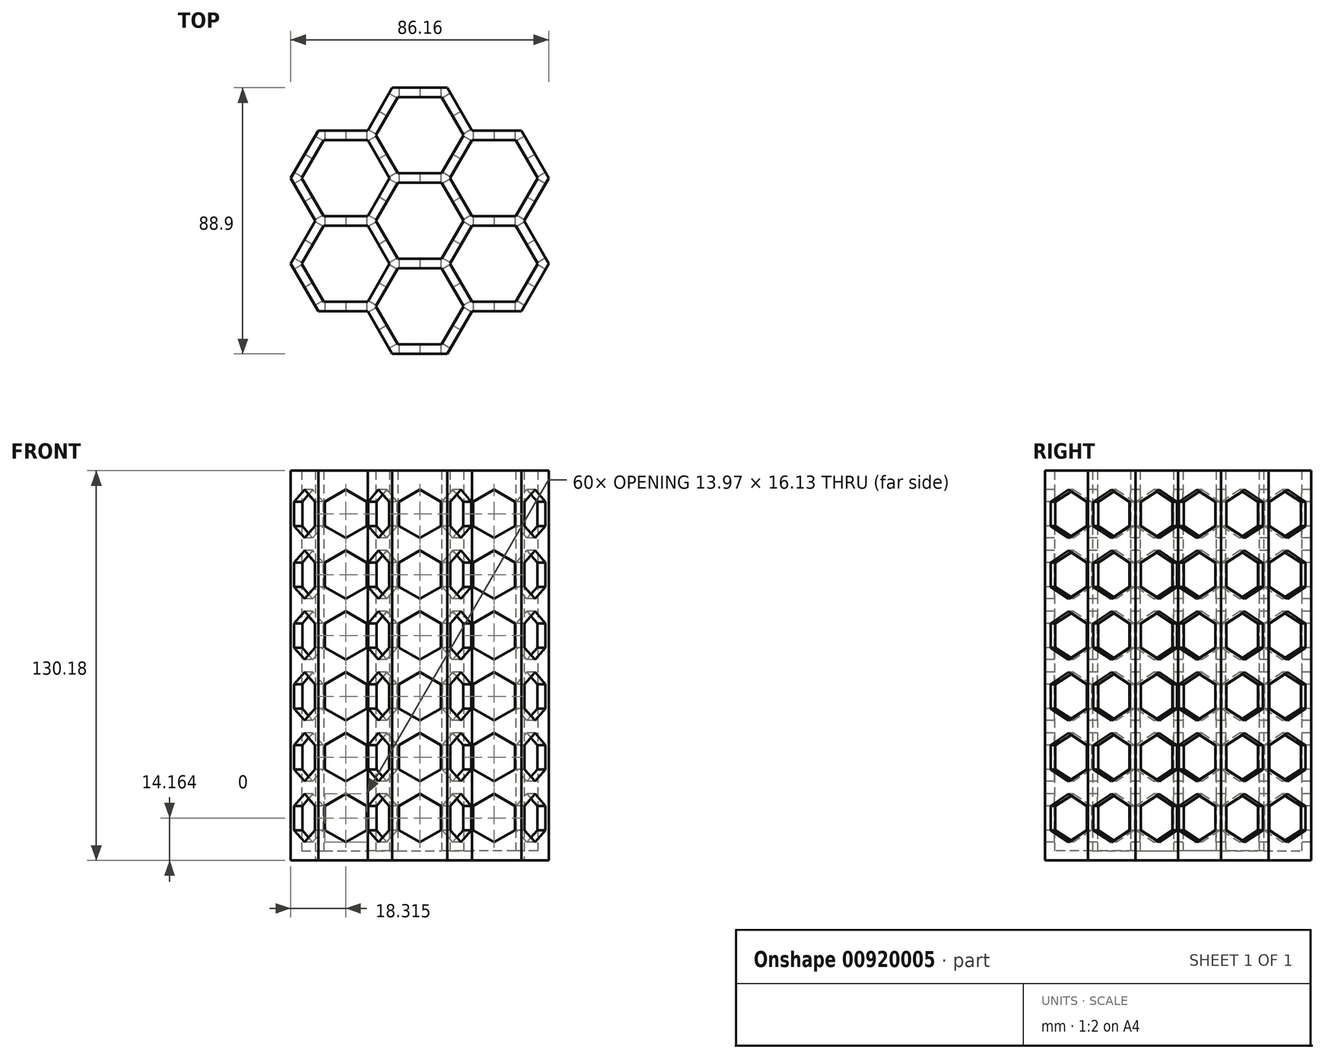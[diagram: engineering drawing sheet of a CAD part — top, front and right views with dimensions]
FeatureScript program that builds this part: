
annotation { "Feature Type Name" : "Feature", "Feature Type Description" : "" }
export const myFeature = defineFeature(function(context is Context, id is Id, definition is map)
    precondition{}
    {
        {
            var Q0;
            Q0=qCreatedBy(makeId("Top.planeOp"),FACE);
            var sketch = newSketch(context, id + "F0", { "sketchPlane" : qUnion([Q0])});
            skCircle(sketch, "E0.cCircle", {"center": v(0, 0) * mm, "radius": 12.7 * mm, "construction": true});
            skLineSegment(sketch, "E0.0", {"start": v(-7.33, 12.7) * mm, "end": v(7.33, 12.7) * mm});
            skLineSegment(sketch, "E0.1", {"start": v(7.33, 12.7) * mm, "end": v(14.66, 0) * mm});
            skLineSegment(sketch, "E0.2", {"start": v(14.66, 0) * mm, "end": v(7.33, -12.7) * mm});
            skLineSegment(sketch, "E0.3", {"start": v(7.33, -12.7) * mm, "end": v(-7.33, -12.7) * mm});
            skLineSegment(sketch, "E0.4", {"start": v(-7.33, -12.7) * mm, "end": v(-14.66, 0) * mm});
            skLineSegment(sketch, "E0.5", {"start": v(-14.66, 0) * mm, "end": v(-7.33, 12.7) * mm});
            skPoint(sketch, "E0.0.midPoint", {"position": v(0, 12.7) * mm});
            skLineSegment(sketch, "E1.0", {"start": v(8.25, -14.29) * mm, "end": v(-8.25, -14.29) * mm});
            skLineSegment(sketch, "E1.1", {"start": v(-16.5, 0) * mm, "end": v(-8.25, 14.29) * mm});
            skLineSegment(sketch, "E1.2", {"start": v(-8.25, 14.29) * mm, "end": v(8.25, 14.29) * mm});
            skLineSegment(sketch, "E1.3", {"start": v(-8.25, -14.29) * mm, "end": v(-16.5, 0) * mm});
            skLineSegment(sketch, "E1.4", {"start": v(8.25, 14.29) * mm, "end": v(16.5, 0) * mm});
            skLineSegment(sketch, "E1.5", {"start": v(16.5, 0) * mm, "end": v(8.25, -14.29) * mm});
            skLineSegment(sketch, "E2.MirrorCS", {"start": v(-7.33, 15.88) * mm, "end": v(7.33, 15.88) * mm});
            skLineSegment(sketch, "E3.MirrorCS", {"start": v(8.25, 14.29) * mm, "end": v(16.5, 28.57) * mm});
            skLineSegment(sketch, "E4.MirrorCS", {"start": v(7.33, 15.88) * mm, "end": v(14.66, 28.58) * mm});
            skLineSegment(sketch, "E5.MirrorCS", {"start": v(16.5, 28.57) * mm, "end": v(8.25, 42.86) * mm});
            skLineSegment(sketch, "E6.MirrorCS", {"start": v(14.66, 28.57) * mm, "end": v(7.33, 41.28) * mm});
            skLineSegment(sketch, "E7.MirrorCS", {"start": v(8.25, 42.86) * mm, "end": v(-8.25, 42.86) * mm});
            skLineSegment(sketch, "E8.MirrorCS", {"start": v(7.33, 41.28) * mm, "end": v(-7.33, 41.28) * mm});
            skLineSegment(sketch, "E9.MirrorCS", {"start": v(-8.25, 42.86) * mm, "end": v(-16.5, 28.57) * mm});
            skLineSegment(sketch, "E10.MirrorCS", {"start": v(-7.33, 41.28) * mm, "end": v(-14.66, 28.58) * mm});
            skLineSegment(sketch, "E11.MirrorCS", {"start": v(-16.5, 28.57) * mm, "end": v(-8.25, 14.29) * mm});
            skLineSegment(sketch, "E12.MirrorCS", {"start": v(-14.66, 28.58) * mm, "end": v(-7.33, 15.88) * mm});
            skLineSegment(sketch, "E13.1.0", {"start": v(-16.5, 28.58) * mm, "end": v(-33, 28.58) * mm});
            skLineSegment(sketch, "E13.1.1", {"start": v(-41.24, 14.29) * mm, "end": v(-33, 0) * mm});
            skLineSegment(sketch, "E13.1.2", {"start": v(-17.41, 26.99) * mm, "end": v(-32.08, 26.99) * mm});
            skLineSegment(sketch, "E13.1.3", {"start": v(-32.08, 26.99) * mm, "end": v(-39.41, 14.29) * mm});
            skLineSegment(sketch, "E13.1.4", {"start": v(-32.08, 1.59) * mm, "end": v(-17.41, 1.59) * mm});
            skLineSegment(sketch, "E13.1.5", {"start": v(-17.41, 1.59) * mm, "end": v(-10.08, 14.29) * mm});
            skLineSegment(sketch, "E13.1.6", {"start": v(-10.08, 14.29) * mm, "end": v(-17.41, 26.99) * mm});
            skLineSegment(sketch, "E13.1.7", {"start": v(-33, 28.57) * mm, "end": v(-41.24, 14.29) * mm});
            skLineSegment(sketch, "E13.1.8", {"start": v(-8.25, 14.29) * mm, "end": v(-16.5, 28.58) * mm});
            skLineSegment(sketch, "E13.1.9", {"start": v(-33, 0) * mm, "end": v(-16.5, 0) * mm});
            skLineSegment(sketch, "E13.1.10", {"start": v(-39.41, 14.29) * mm, "end": v(-32.08, 1.59) * mm});
            skLineSegment(sketch, "E13.2.0", {"start": v(-33, 0) * mm, "end": v(-41.24, -14.29) * mm});
            skLineSegment(sketch, "E13.2.1", {"start": v(-33, -28.57) * mm, "end": v(-16.5, -28.57) * mm});
            skLineSegment(sketch, "E13.2.2", {"start": v(-32.08, -1.59) * mm, "end": v(-39.41, -14.29) * mm});
            skLineSegment(sketch, "E13.2.3", {"start": v(-39.41, -14.29) * mm, "end": v(-32.08, -26.99) * mm});
            skLineSegment(sketch, "E13.2.4", {"start": v(-17.41, -26.99) * mm, "end": v(-10.08, -14.29) * mm});
            skLineSegment(sketch, "E13.2.5", {"start": v(-10.08, -14.29) * mm, "end": v(-17.41, -1.59) * mm});
            skLineSegment(sketch, "E13.2.6", {"start": v(-17.41, -1.59) * mm, "end": v(-32.08, -1.59) * mm});
            skLineSegment(sketch, "E13.2.7", {"start": v(-41.24, -14.29) * mm, "end": v(-33, -28.57) * mm});
            skLineSegment(sketch, "E13.2.8", {"start": v(-16.5, 0) * mm, "end": v(-33, 0) * mm});
            skLineSegment(sketch, "E13.2.9", {"start": v(-16.5, -28.57) * mm, "end": v(-8.25, -14.29) * mm});
            skLineSegment(sketch, "E13.2.10", {"start": v(-32.08, -26.99) * mm, "end": v(-17.41, -26.99) * mm});
            skLineSegment(sketch, "E13.3.0", {"start": v(-16.5, -28.57) * mm, "end": v(-8.25, -42.86) * mm});
            skLineSegment(sketch, "E13.3.1", {"start": v(8.25, -42.86) * mm, "end": v(16.5, -28.57) * mm});
            skLineSegment(sketch, "E13.3.2", {"start": v(-14.66, -28.57) * mm, "end": v(-7.33, -41.27) * mm});
            skLineSegment(sketch, "E13.3.3", {"start": v(-7.33, -41.27) * mm, "end": v(7.33, -41.27) * mm});
            skLineSegment(sketch, "E13.3.4", {"start": v(14.66, -28.57) * mm, "end": v(7.33, -15.88) * mm});
            skLineSegment(sketch, "E13.3.5", {"start": v(7.33, -15.88) * mm, "end": v(-7.33, -15.88) * mm});
            skLineSegment(sketch, "E13.3.6", {"start": v(-7.33, -15.88) * mm, "end": v(-14.66, -28.58) * mm});
            skLineSegment(sketch, "E13.3.7", {"start": v(-8.25, -42.86) * mm, "end": v(8.25, -42.86) * mm});
            skLineSegment(sketch, "E13.3.8", {"start": v(-8.25, -14.29) * mm, "end": v(-16.5, -28.58) * mm});
            skLineSegment(sketch, "E13.3.9", {"start": v(16.5, -28.57) * mm, "end": v(8.25, -14.29) * mm});
            skLineSegment(sketch, "E13.3.10", {"start": v(7.33, -41.28) * mm, "end": v(14.66, -28.58) * mm});
            skLineSegment(sketch, "E13.4.0", {"start": v(16.5, -28.58) * mm, "end": v(33, -28.58) * mm});
            skLineSegment(sketch, "E13.4.1", {"start": v(41.24, -14.29) * mm, "end": v(33, 0) * mm});
            skLineSegment(sketch, "E13.4.2", {"start": v(17.41, -26.99) * mm, "end": v(32.08, -26.99) * mm});
            skLineSegment(sketch, "E13.4.3", {"start": v(32.08, -26.99) * mm, "end": v(39.41, -14.29) * mm});
            skLineSegment(sketch, "E13.4.4", {"start": v(32.08, -1.59) * mm, "end": v(17.41, -1.59) * mm});
            skLineSegment(sketch, "E13.4.5", {"start": v(17.41, -1.59) * mm, "end": v(10.08, -14.29) * mm});
            skLineSegment(sketch, "E13.4.6", {"start": v(10.08, -14.29) * mm, "end": v(17.41, -26.99) * mm});
            skLineSegment(sketch, "E13.4.7", {"start": v(33, -28.57) * mm, "end": v(41.24, -14.29) * mm});
            skLineSegment(sketch, "E13.4.8", {"start": v(8.25, -14.29) * mm, "end": v(16.5, -28.57) * mm});
            skLineSegment(sketch, "E13.4.9", {"start": v(33, 0) * mm, "end": v(16.5, 0) * mm});
            skLineSegment(sketch, "E13.4.10", {"start": v(39.41, -14.29) * mm, "end": v(32.08, -1.59) * mm});
            skLineSegment(sketch, "E13.5.0", {"start": v(33, 0) * mm, "end": v(41.24, 14.29) * mm});
            skLineSegment(sketch, "E13.5.1", {"start": v(33, 28.57) * mm, "end": v(16.5, 28.57) * mm});
            skLineSegment(sketch, "E13.5.2", {"start": v(32.08, 1.59) * mm, "end": v(39.41, 14.29) * mm});
            skLineSegment(sketch, "E13.5.3", {"start": v(39.41, 14.29) * mm, "end": v(32.08, 26.99) * mm});
            skLineSegment(sketch, "E13.5.4", {"start": v(17.41, 26.99) * mm, "end": v(10.08, 14.29) * mm});
            skLineSegment(sketch, "E13.5.5", {"start": v(10.08, 14.29) * mm, "end": v(17.41, 1.59) * mm});
            skLineSegment(sketch, "E13.5.6", {"start": v(17.41, 1.59) * mm, "end": v(32.08, 1.59) * mm});
            skLineSegment(sketch, "E13.5.7", {"start": v(41.24, 14.29) * mm, "end": v(33, 28.57) * mm});
            skLineSegment(sketch, "E13.5.8", {"start": v(16.5, 0) * mm, "end": v(33, 0) * mm});
            skLineSegment(sketch, "E13.5.9", {"start": v(16.5, 28.57) * mm, "end": v(8.25, 14.29) * mm});
            skLineSegment(sketch, "E13.5.10", {"start": v(32.08, 26.99) * mm, "end": v(17.41, 26.99) * mm});
            skLineSegment(sketch, "E14.0", {"start": v(-17.41, -30.16) * mm, "end": v(-9.17, -44.45) * mm});
            skLineSegment(sketch, "E14.1", {"start": v(-33.91, -30.16) * mm, "end": v(-17.41, -30.16) * mm});
            skLineSegment(sketch, "E14.2", {"start": v(-43.08, -14.29) * mm, "end": v(-33.91, -30.16) * mm});
            skLineSegment(sketch, "E14.3", {"start": v(-34.83, 0) * mm, "end": v(-43.08, -14.29) * mm});
            skLineSegment(sketch, "E14.4", {"start": v(-43.08, 14.29) * mm, "end": v(-34.83, 0) * mm});
            skLineSegment(sketch, "E14.5", {"start": v(-9.17, -44.45) * mm, "end": v(9.17, -44.45) * mm});
            skLineSegment(sketch, "E14.6", {"start": v(-33.91, 30.16) * mm, "end": v(-43.08, 14.29) * mm});
            skLineSegment(sketch, "E14.7", {"start": v(-17.41, 30.16) * mm, "end": v(-33.91, 30.16) * mm});
            skLineSegment(sketch, "E14.8", {"start": v(43.08, -14.29) * mm, "end": v(34.83, 0) * mm});
            skLineSegment(sketch, "E14.9", {"start": v(33.91, -30.16) * mm, "end": v(43.08, -14.29) * mm});
            skLineSegment(sketch, "E14.10", {"start": v(17.41, -30.16) * mm, "end": v(33.91, -30.16) * mm});
            skLineSegment(sketch, "E14.11", {"start": v(9.17, -44.45) * mm, "end": v(17.41, -30.16) * mm});
            skLineSegment(sketch, "E14.12", {"start": v(34.83, 0) * mm, "end": v(43.08, 14.29) * mm});
            skLineSegment(sketch, "E14.13", {"start": v(43.08, 14.29) * mm, "end": v(33.91, 30.16) * mm});
            skLineSegment(sketch, "E14.14", {"start": v(33.91, 30.16) * mm, "end": v(17.41, 30.16) * mm});
            skLineSegment(sketch, "E14.15", {"start": v(17.41, 30.16) * mm, "end": v(9.17, 44.45) * mm});
            skLineSegment(sketch, "E14.16", {"start": v(9.17, 44.45) * mm, "end": v(-9.17, 44.45) * mm});
            skLineSegment(sketch, "E14.17", {"start": v(-9.17, 44.45) * mm, "end": v(-17.41, 30.16) * mm});
            skSolve(sketch);
        }
        {
            var Q0;
            Q0 = qSketchRegion(id + "F0", true);
            var Q1;
            Q1=makeQuery(id+"F0.imprint","IMPRINT",FACE,{"disambiguationData":[TD([[makeQuery(id+"F0.imprint","IMPRINT",EDGE,{"derivedFrom":sQuery(id+"F0.wireOp",EDGE,"E0.0")}),1.0]])]});
            var Q2;
            Q2=makeQuery(id+"F0.imprint","IMPRINT",FACE,{"disambiguationData":[TD([[makeQuery(id+"F0.imprint","IMPRINT",EDGE,{"derivedFrom":sQuery(id+"F0.wireOp",EDGE,"E1.3")}),1.0]])]});
            var Q3;
            Q3=makeQuery(id+"F0.imprint","IMPRINT",FACE,{"disambiguationData":[TD([[makeQuery(id+"F0.imprint","IMPRINT",EDGE,{"derivedFrom":sQuery(id+"F0.wireOp",EDGE,"E1.0")}),1.0]])]});
            var Q4;
            Q4=makeQuery(id+"F0.imprint","IMPRINT",FACE,{"disambiguationData":[TD([[makeQuery(id+"F0.imprint","IMPRINT",EDGE,{"derivedFrom":sQuery(id+"F0.wireOp",EDGE,"E1.5")}),1.0]])]});
            var Q5;
            Q5=makeQuery(id+"F0.imprint","IMPRINT",FACE,{"disambiguationData":[TD([[makeQuery(id+"F0.imprint","IMPRINT",EDGE,{"derivedFrom":sQuery(id+"F0.wireOp",EDGE,"E1.4")}),1.0]])]});
            var Q6;
            Q6=makeQuery(id+"F0.imprint","IMPRINT",FACE,{"disambiguationData":[TD([[makeQuery(id+"F0.imprint","IMPRINT",EDGE,{"derivedFrom":sQuery(id+"F0.wireOp",EDGE,"E1.2")}),1.0]])]});
            var Q7;
            Q7=makeQuery(id+"F0.imprint","IMPRINT",FACE,{"disambiguationData":[TD([[makeQuery(id+"F0.imprint","IMPRINT",EDGE,{"derivedFrom":sQuery(id+"F0.wireOp",EDGE,"E1.1")}),1.0]])]});
            extrude(context, id + "F1", {"entities" : qUnion([Q0, Q1, Q2, Q3, Q4, Q5, Q6, Q7]), "depth" : 127 * mm, "offsetDistance" : 25.4 * mm});
        }
        {
            var Q0;
            Q0=makeQuery(id+"F1.opExtrude","CAP_FACE",FACE,{"disambiguationData":[OSD([sQuery(id+"F0.wireOp",EDGE,"E0.0"),sQuery(id+"F0.wireOp",EDGE,"E0.1"),sQuery(id+"F0.wireOp",EDGE,"E0.2"),sQuery(id+"F0.wireOp",EDGE,"E0.3"),sQuery(id+"F0.wireOp",EDGE,"E0.4"),sQuery(id+"F0.wireOp",EDGE,"E0.5"),sQuery(id+"F0.wireOp",EDGE,"E2.MirrorCS"),sQuery(id+"F0.wireOp",EDGE,"E4.MirrorCS"),sQuery(id+"F0.wireOp",EDGE,"E5.MirrorCS"),sQuery(id+"F0.wireOp",EDGE,"E6.MirrorCS"),sQuery(id+"F0.wireOp",EDGE,"E7.MirrorCS"),sQuery(id+"F0.wireOp",EDGE,"E8.MirrorCS"),sQuery(id+"F0.wireOp",EDGE,"E9.MirrorCS"),sQuery(id+"F0.wireOp",EDGE,"E10.MirrorCS"),sQuery(id+"F0.wireOp",EDGE,"E12.MirrorCS"),sQuery(id+"F0.wireOp",EDGE,"E13.1.0"),sQuery(id+"F0.wireOp",EDGE,"E13.1.1"),sQuery(id+"F0.wireOp",EDGE,"E13.1.2"),sQuery(id+"F0.wireOp",EDGE,"E13.1.3"),sQuery(id+"F0.wireOp",EDGE,"E13.1.4"),sQuery(id+"F0.wireOp",EDGE,"E13.1.5"),sQuery(id+"F0.wireOp",EDGE,"E13.1.6"),sQuery(id+"F0.wireOp",EDGE,"E13.1.7"),sQuery(id+"F0.wireOp",EDGE,"E13.1.10"),sQuery(id+"F0.wireOp",EDGE,"E13.2.0"),sQuery(id+"F0.wireOp",EDGE,"E13.2.1"),sQuery(id+"F0.wireOp",EDGE,"E13.2.2"),sQuery(id+"F0.wireOp",EDGE,"E13.2.3"),sQuery(id+"F0.wireOp",EDGE,"E13.2.4"),sQuery(id+"F0.wireOp",EDGE,"E13.2.5"),sQuery(id+"F0.wireOp",EDGE,"E13.2.6"),sQuery(id+"F0.wireOp",EDGE,"E13.2.7"),sQuery(id+"F0.wireOp",EDGE,"E13.2.10"),sQuery(id+"F0.wireOp",EDGE,"E13.3.0"),sQuery(id+"F0.wireOp",EDGE,"E13.3.1"),sQuery(id+"F0.wireOp",EDGE,"E13.3.2"),sQuery(id+"F0.wireOp",EDGE,"E13.3.3"),sQuery(id+"F0.wireOp",EDGE,"E13.3.4"),sQuery(id+"F0.wireOp",EDGE,"E13.3.5"),sQuery(id+"F0.wireOp",EDGE,"E13.3.6"),sQuery(id+"F0.wireOp",EDGE,"E13.3.7"),sQuery(id+"F0.wireOp",EDGE,"E13.3.10"),sQuery(id+"F0.wireOp",EDGE,"E13.4.0"),sQuery(id+"F0.wireOp",EDGE,"E13.4.1"),sQuery(id+"F0.wireOp",EDGE,"E13.4.2"),sQuery(id+"F0.wireOp",EDGE,"E13.4.3"),sQuery(id+"F0.wireOp",EDGE,"E13.4.4"),sQuery(id+"F0.wireOp",EDGE,"E13.4.5"),sQuery(id+"F0.wireOp",EDGE,"E13.4.6"),sQuery(id+"F0.wireOp",EDGE,"E13.4.7"),sQuery(id+"F0.wireOp",EDGE,"E13.4.10"),sQuery(id+"F0.wireOp",EDGE,"E13.5.0"),sQuery(id+"F0.wireOp",EDGE,"E13.5.1"),sQuery(id+"F0.wireOp",EDGE,"E13.5.2"),sQuery(id+"F0.wireOp",EDGE,"E13.5.3"),sQuery(id+"F0.wireOp",EDGE,"E13.5.4"),sQuery(id+"F0.wireOp",EDGE,"E13.5.5"),sQuery(id+"F0.wireOp",EDGE,"E13.5.6"),sQuery(id+"F0.wireOp",EDGE,"E13.5.7"),sQuery(id+"F0.wireOp",EDGE,"E13.5.10")])],"isStart":true});
            var sketch = newSketch(context, id + "F2", { "sketchPlane" : qUnion([Q0])});
            skLineSegment(sketch, "E15", {"start": v(-33.91, 30.16) * mm, "end": v(-17.41, 30.16) * mm});
            skLineSegment(sketch, "E16", {"start": v(-17.41, 30.16) * mm, "end": v(-9.17, 44.45) * mm});
            skLineSegment(sketch, "E17", {"start": v(-9.17, 44.45) * mm, "end": v(9.17, 44.45) * mm});
            skLineSegment(sketch, "E18", {"start": v(9.17, 44.45) * mm, "end": v(17.41, 30.16) * mm});
            skLineSegment(sketch, "E19", {"start": v(17.41, 30.16) * mm, "end": v(33.91, 30.16) * mm});
            skLineSegment(sketch, "E20", {"start": v(33.91, 30.16) * mm, "end": v(43.08, 14.29) * mm});
            skLineSegment(sketch, "E21", {"start": v(43.08, 14.29) * mm, "end": v(34.83, 0) * mm});
            skLineSegment(sketch, "E22", {"start": v(34.83, 0) * mm, "end": v(43.08, -14.29) * mm});
            skLineSegment(sketch, "E23", {"start": v(43.08, -14.29) * mm, "end": v(33.91, -30.16) * mm});
            skLineSegment(sketch, "E24", {"start": v(33.91, -30.16) * mm, "end": v(17.41, -30.16) * mm});
            skLineSegment(sketch, "E25", {"start": v(17.41, -30.16) * mm, "end": v(9.17, -44.45) * mm});
            skLineSegment(sketch, "E26", {"start": v(9.17, -44.45) * mm, "end": v(-9.17, -44.45) * mm});
            skLineSegment(sketch, "E27", {"start": v(-9.17, -44.45) * mm, "end": v(-17.41, -30.16) * mm});
            skLineSegment(sketch, "E28", {"start": v(-17.41, -30.16) * mm, "end": v(-33.91, -30.16) * mm});
            skLineSegment(sketch, "E29", {"start": v(-33.91, -30.16) * mm, "end": v(-43.08, -14.29) * mm});
            skLineSegment(sketch, "E30", {"start": v(-43.08, -14.29) * mm, "end": v(-34.83, 0) * mm});
            skLineSegment(sketch, "E31", {"start": v(-34.83, 0) * mm, "end": v(-43.08, 14.29) * mm});
            skLineSegment(sketch, "E32", {"start": v(-43.08, 14.29) * mm, "end": v(-33.91, 30.16) * mm});
            skSolve(sketch);
        }
        {
            var Q0;
            Q0 = qSketchRegion(id + "F2", true);
            extrude(context, id + "F3", {"entities" : qUnion([Q0]), "operationType" : NewBodyOperationType.ADD, "depth" : 3.17 * mm, "offsetDistance" : 25.4 * mm});
        }
        {
            var Q0;
            Q0=makeQuery(id+"F3.boolean.opBoolean","MERGE",EDGE,{"derivedFrom":[makeQuery(id+"F1.opExtrude","SWEPT_EDGE",EDGE,{"disambiguationData":[OSD([sQuery(id+"F0.wireOp",EDGE,"E14.7"),sQuery(id+"F0.wireOp",EDGE,"E14.17")])]}),makeQuery(id+"F3.opExtrude","SWEPT_EDGE",EDGE,{"disambiguationData":[OSD([sQuery(id+"F2.wireOp",EDGE,"E27"),sQuery(id+"F2.wireOp",EDGE,"E28")])]})]});
            var Q1;
            Q1=makeQuery(id+"F3.boolean.opBoolean","MERGE",EDGE,{"derivedFrom":[makeQuery(id+"F1.opExtrude","SWEPT_EDGE",EDGE,{"disambiguationData":[OSD([sQuery(id+"F0.wireOp",EDGE,"E14.10"),sQuery(id+"F0.wireOp",EDGE,"E14.11")])]}),makeQuery(id+"F3.opExtrude","SWEPT_EDGE",EDGE,{"disambiguationData":[OSD([sQuery(id+"F2.wireOp",EDGE,"E18"),sQuery(id+"F2.wireOp",EDGE,"E19")])]})]});
            cPlane(context, id + "F4", {"entities" : qUnion([Q0, Q1]), "cplaneType" : CPlaneType.LINE_ANGLE, "offset" : 25.4 * mm, "angle" : 0 * degree, "width" : 152.4 * mm, "height" : 152.4 * mm});
        }
        {
            var Q0;
            Q0=qCreatedBy(id+"F4.planeOp",FACE);
            var sketch = newSketch(context, id + "F5", { "sketchPlane" : qUnion([Q0])});
            skCircle(sketch, "E33.cCircle", {"center": v(0, 112.58) * mm, "radius": 6.99 * mm, "construction": true});
            skPoint(sketch, "E33.cCircle.centerSnap0", {"position": v(0, 127) * mm});
            skLineSegment(sketch, "E33.0", {"start": v(-6.99, 108.55) * mm, "end": v(-6.99, 116.62) * mm});
            skLineSegment(sketch, "E33.1", {"start": v(-6.99, 116.62) * mm, "end": v(0, 120.65) * mm});
            skLineSegment(sketch, "E33.2", {"start": v(0, 120.65) * mm, "end": v(6.99, 116.62) * mm});
            skLineSegment(sketch, "E33.3", {"start": v(6.99, 116.62) * mm, "end": v(6.99, 108.55) * mm});
            skLineSegment(sketch, "E33.4", {"start": v(6.98, 108.55) * mm, "end": v(0, 104.52) * mm});
            skLineSegment(sketch, "E33.5", {"start": v(0, 104.52) * mm, "end": v(-6.99, 108.55) * mm});
            skPoint(sketch, "E34.1.0.0", {"position": v(0, 106.68) * mm});
            skLineSegment(sketch, "E34.1.0.1", {"start": v(6.99, 96.3) * mm, "end": v(6.99, 88.23) * mm});
            skCircle(sketch, "E34.1.0.3", {"center": v(0, 92.26) * mm, "radius": 6.99 * mm, "construction": true});
            skLineSegment(sketch, "E34.1.0.4", {"start": v(0, 100.33) * mm, "end": v(6.99, 96.3) * mm});
            skLineSegment(sketch, "E34.1.0.5", {"start": v(-6.99, 96.3) * mm, "end": v(0, 100.33) * mm});
            skLineSegment(sketch, "E34.1.0.6", {"start": v(-6.99, 88.23) * mm, "end": v(-6.99, 96.3) * mm});
            skLineSegment(sketch, "E34.1.0.7", {"start": v(0, 84.2) * mm, "end": v(-6.98, 88.23) * mm});
            skLineSegment(sketch, "E34.1.0.8", {"start": v(6.99, 88.23) * mm, "end": v(0, 84.2) * mm});
            skPoint(sketch, "E34.2.0.0", {"position": v(0, 86.36) * mm});
            skLineSegment(sketch, "E34.2.0.1", {"start": v(6.99, 75.98) * mm, "end": v(6.99, 67.91) * mm});
            skCircle(sketch, "E34.2.0.3", {"center": v(0, 71.94) * mm, "radius": 6.99 * mm, "construction": true});
            skLineSegment(sketch, "E34.2.0.4", {"start": v(0, 80.01) * mm, "end": v(6.99, 75.98) * mm});
            skLineSegment(sketch, "E34.2.0.5", {"start": v(-6.99, 75.98) * mm, "end": v(0, 80) * mm});
            skLineSegment(sketch, "E34.2.0.6", {"start": v(-6.99, 67.91) * mm, "end": v(-6.99, 75.98) * mm});
            skLineSegment(sketch, "E34.2.0.7", {"start": v(0, 63.88) * mm, "end": v(-6.98, 67.91) * mm});
            skLineSegment(sketch, "E34.2.0.8", {"start": v(6.99, 67.91) * mm, "end": v(0, 63.88) * mm});
            skPoint(sketch, "E34.3.0.0", {"position": v(0, 66.04) * mm});
            skLineSegment(sketch, "E34.3.0.1", {"start": v(6.99, 55.66) * mm, "end": v(6.99, 47.6) * mm});
            skCircle(sketch, "E34.3.0.3", {"center": v(0, 51.62) * mm, "radius": 6.99 * mm, "construction": true});
            skLineSegment(sketch, "E34.3.0.4", {"start": v(0, 59.7) * mm, "end": v(6.99, 55.66) * mm});
            skLineSegment(sketch, "E34.3.0.5", {"start": v(-6.99, 55.66) * mm, "end": v(0, 59.69) * mm});
            skLineSegment(sketch, "E34.3.0.6", {"start": v(-6.99, 47.6) * mm, "end": v(-6.99, 55.66) * mm});
            skLineSegment(sketch, "E34.3.0.7", {"start": v(0, 43.56) * mm, "end": v(-6.98, 47.6) * mm});
            skLineSegment(sketch, "E34.3.0.8", {"start": v(6.99, 47.6) * mm, "end": v(0, 43.56) * mm});
            skPoint(sketch, "E34.4.0.0", {"position": v(0, 45.72) * mm});
            skLineSegment(sketch, "E34.4.0.1", {"start": v(6.99, 35.34) * mm, "end": v(6.99, 27.27) * mm});
            skCircle(sketch, "E34.4.0.3", {"center": v(0, 31.3) * mm, "radius": 6.99 * mm, "construction": true});
            skLineSegment(sketch, "E34.4.0.4", {"start": v(0, 39.37) * mm, "end": v(6.99, 35.34) * mm});
            skLineSegment(sketch, "E34.4.0.5", {"start": v(-6.99, 35.34) * mm, "end": v(0, 39.37) * mm});
            skLineSegment(sketch, "E34.4.0.6", {"start": v(-6.99, 27.27) * mm, "end": v(-6.99, 35.34) * mm});
            skLineSegment(sketch, "E34.4.0.7", {"start": v(0, 23.24) * mm, "end": v(-6.98, 27.27) * mm});
            skLineSegment(sketch, "E34.4.0.8", {"start": v(6.99, 27.27) * mm, "end": v(0, 23.24) * mm});
            skLineSegment(sketch, "E34.direction1", {"start": v(-6.99, 108.55) * mm, "end": v(-6.99, 88.23) * mm, "construction": true});
            skPoint(sketch, "E35.0.5.0", {"position": v(0, 25.4) * mm});
            skLineSegment(sketch, "E35.1.5.0", {"start": v(6.99, 15.02) * mm, "end": v(6.99, 6.95) * mm});
            skCircle(sketch, "E35.5.5.0", {"center": v(0, 10.98) * mm, "radius": 6.99 * mm, "construction": true});
            skLineSegment(sketch, "E35.7.5.0", {"start": v(0, 19.05) * mm, "end": v(6.98, 15.02) * mm});
            skLineSegment(sketch, "E35.10.5.0", {"start": v(-6.99, 15.02) * mm, "end": v(0, 19.05) * mm});
            skLineSegment(sketch, "E35.13.5.0", {"start": v(-6.99, 6.95) * mm, "end": v(-6.99, 15.02) * mm});
            skLineSegment(sketch, "E35.16.5.0", {"start": v(0, 2.92) * mm, "end": v(-6.98, 6.95) * mm});
            skLineSegment(sketch, "E35.19.5.0", {"start": v(6.99, 6.95) * mm, "end": v(0, 2.92) * mm});
            skLineSegment(sketch, "E36", {"start": v(0, 127) * mm, "end": v(0, 112.58) * mm});
            skCircle(sketch, "E37.1.0.0", {"center": v(24.76, 112.58) * mm, "radius": 6.99 * mm, "construction": true});
            skPoint(sketch, "E37.1.0.1", {"position": v(24.76, 86.36) * mm});
            skCircle(sketch, "E37.1.0.2", {"center": v(24.76, 71.94) * mm, "radius": 6.99 * mm, "construction": true});
            skLineSegment(sketch, "E37.1.0.3", {"start": v(17.78, 96.3) * mm, "end": v(24.76, 100.33) * mm});
            skPoint(sketch, "E37.1.0.4", {"position": v(24.76, 106.68) * mm});
            skLineSegment(sketch, "E37.1.0.5", {"start": v(31.75, 55.66) * mm, "end": v(31.75, 47.6) * mm});
            skLineSegment(sketch, "E37.1.0.6", {"start": v(24.76, 127) * mm, "end": v(24.76, 112.58) * mm});
            skPoint(sketch, "E37.1.0.7", {"position": v(24.76, 45.72) * mm});
            skLineSegment(sketch, "E37.1.0.8", {"start": v(31.75, 108.55) * mm, "end": v(24.76, 104.52) * mm});
            skLineSegment(sketch, "E37.1.0.9", {"start": v(17.78, 6.95) * mm, "end": v(17.78, 15.02) * mm});
            skCircle(sketch, "E37.1.0.10", {"center": v(24.76, 51.62) * mm, "radius": 6.99 * mm, "construction": true});
            skCircle(sketch, "E37.1.0.11", {"center": v(24.76, 10.98) * mm, "radius": 6.99 * mm, "construction": true});
            skLineSegment(sketch, "E37.1.0.12", {"start": v(17.78, 108.55) * mm, "end": v(17.78, 88.23) * mm, "construction": true});
            skLineSegment(sketch, "E37.1.0.13", {"start": v(24.76, 39.37) * mm, "end": v(31.75, 35.34) * mm});
            skLineSegment(sketch, "E37.1.0.14", {"start": v(31.75, 6.95) * mm, "end": v(24.76, 2.92) * mm});
            skLineSegment(sketch, "E37.1.0.15", {"start": v(17.78, 116.62) * mm, "end": v(24.76, 120.65) * mm});
            skLineSegment(sketch, "E37.1.0.16", {"start": v(17.78, 55.66) * mm, "end": v(24.76, 59.69) * mm});
            skCircle(sketch, "E37.1.0.17", {"center": v(24.76, 92.26) * mm, "radius": 6.99 * mm, "construction": true});
            skLineSegment(sketch, "E37.1.0.18", {"start": v(17.78, 15.02) * mm, "end": v(24.76, 19.05) * mm});
            skLineSegment(sketch, "E37.1.0.19", {"start": v(24.76, 84.2) * mm, "end": v(17.78, 88.23) * mm});
            skPoint(sketch, "E37.1.0.20", {"position": v(24.76, 25.4) * mm});
            skPoint(sketch, "E37.1.0.21", {"position": v(24.76, 66.04) * mm});
            skCircle(sketch, "E37.1.0.22", {"center": v(24.76, 31.3) * mm, "radius": 6.99 * mm, "construction": true});
            skLineSegment(sketch, "E37.1.0.23", {"start": v(24.76, 43.56) * mm, "end": v(17.78, 47.6) * mm});
            skLineSegment(sketch, "E37.1.0.24", {"start": v(31.75, 27.27) * mm, "end": v(24.76, 23.24) * mm});
            skLineSegment(sketch, "E37.1.0.25", {"start": v(31.75, 67.91) * mm, "end": v(24.76, 63.88) * mm});
            skLineSegment(sketch, "E37.1.0.26", {"start": v(17.78, 27.27) * mm, "end": v(17.78, 35.34) * mm});
            skLineSegment(sketch, "E37.1.0.27", {"start": v(24.76, 63.88) * mm, "end": v(17.78, 67.91) * mm});
            skLineSegment(sketch, "E37.1.0.28", {"start": v(24.76, 120.65) * mm, "end": v(31.75, 116.62) * mm});
            skLineSegment(sketch, "E37.1.0.29", {"start": v(17.78, 88.23) * mm, "end": v(17.78, 96.3) * mm});
            skLineSegment(sketch, "E37.1.0.30", {"start": v(24.77, 2.92) * mm, "end": v(17.78, 6.95) * mm});
            skLineSegment(sketch, "E37.1.0.31", {"start": v(31.75, 96.3) * mm, "end": v(31.75, 88.23) * mm});
            skLineSegment(sketch, "E37.1.0.32", {"start": v(31.75, 47.6) * mm, "end": v(24.76, 43.56) * mm});
            skLineSegment(sketch, "E37.1.0.33", {"start": v(24.76, 23.24) * mm, "end": v(17.78, 27.27) * mm});
            skLineSegment(sketch, "E37.1.0.34", {"start": v(24.76, 59.7) * mm, "end": v(31.75, 55.66) * mm});
            skLineSegment(sketch, "E37.1.0.35", {"start": v(17.78, 35.34) * mm, "end": v(24.76, 39.37) * mm});
            skLineSegment(sketch, "E37.1.0.36", {"start": v(17.78, 67.91) * mm, "end": v(17.78, 75.98) * mm});
            skLineSegment(sketch, "E37.1.0.37", {"start": v(31.75, 75.98) * mm, "end": v(31.75, 67.91) * mm});
            skLineSegment(sketch, "E37.1.0.38", {"start": v(17.78, 108.55) * mm, "end": v(17.78, 116.62) * mm});
            skLineSegment(sketch, "E37.1.0.39", {"start": v(31.75, 88.23) * mm, "end": v(24.76, 84.2) * mm});
            skLineSegment(sketch, "E37.1.0.40", {"start": v(24.76, 104.52) * mm, "end": v(17.78, 108.55) * mm});
            skLineSegment(sketch, "E37.1.0.41", {"start": v(17.78, 75.98) * mm, "end": v(24.76, 80) * mm});
            skLineSegment(sketch, "E37.1.0.42", {"start": v(31.75, 116.62) * mm, "end": v(31.75, 108.55) * mm});
            skLineSegment(sketch, "E37.1.0.43", {"start": v(24.77, 80) * mm, "end": v(31.75, 75.98) * mm});
            skLineSegment(sketch, "E37.1.0.44", {"start": v(24.76, 100.33) * mm, "end": v(31.75, 96.3) * mm});
            skLineSegment(sketch, "E37.1.0.45", {"start": v(24.76, 19.05) * mm, "end": v(31.75, 15.02) * mm});
            skLineSegment(sketch, "E37.1.0.46", {"start": v(31.75, 15.02) * mm, "end": v(31.75, 6.95) * mm});
            skLineSegment(sketch, "E37.1.0.47", {"start": v(31.75, 35.34) * mm, "end": v(31.75, 27.27) * mm});
            skLineSegment(sketch, "E37.1.0.48", {"start": v(17.78, 47.6) * mm, "end": v(17.78, 55.66) * mm});
            skLineSegment(sketch, "E37.direction1", {"start": v(-6.98, 6.95) * mm, "end": v(17.78, 6.95) * mm, "construction": true});
            skPoint(sketch, "E38.1.0.0", {"position": v(-24.77, 25.4) * mm});
            skLineSegment(sketch, "E38.1.0.1", {"start": v(-24.77, 104.52) * mm, "end": v(-31.75, 108.55) * mm});
            skLineSegment(sketch, "E38.1.0.2", {"start": v(-17.78, 88.23) * mm, "end": v(-24.76, 84.2) * mm});
            skLineSegment(sketch, "E38.1.0.3", {"start": v(-17.78, 6.95) * mm, "end": v(-24.76, 2.92) * mm});
            skLineSegment(sketch, "E38.1.0.4", {"start": v(-31.75, 27.27) * mm, "end": v(-31.75, 35.34) * mm});
            skLineSegment(sketch, "E38.1.0.5", {"start": v(-31.75, 108.55) * mm, "end": v(-31.75, 88.23) * mm, "construction": true});
            skLineSegment(sketch, "E38.1.0.6", {"start": v(-31.75, 108.55) * mm, "end": v(-31.75, 116.62) * mm});
            skLineSegment(sketch, "E38.1.0.7", {"start": v(-24.77, 19.05) * mm, "end": v(-17.78, 15.02) * mm});
            skLineSegment(sketch, "E38.1.0.8", {"start": v(-24.77, 80.01) * mm, "end": v(-17.78, 75.98) * mm});
            skPoint(sketch, "E38.1.0.9", {"position": v(-24.77, 86.36) * mm});
            skLineSegment(sketch, "E38.1.0.10", {"start": v(-31.75, 47.6) * mm, "end": v(-31.75, 55.66) * mm});
            skCircle(sketch, "E38.1.0.11", {"center": v(-24.77, 51.62) * mm, "radius": 6.99 * mm, "construction": true});
            skPoint(sketch, "E38.1.0.12", {"position": v(-24.77, 66.04) * mm});
            skLineSegment(sketch, "E38.1.0.13", {"start": v(-31.75, 75.98) * mm, "end": v(-24.77, 80.01) * mm});
            skLineSegment(sketch, "E38.1.0.14", {"start": v(-31.75, 35.34) * mm, "end": v(-24.77, 39.37) * mm});
            skCircle(sketch, "E38.1.0.15", {"center": v(-24.77, 31.3) * mm, "radius": 6.99 * mm, "construction": true});
            skCircle(sketch, "E38.1.0.16", {"center": v(-24.77, 10.98) * mm, "radius": 6.99 * mm, "construction": true});
            skLineSegment(sketch, "E38.1.0.17", {"start": v(-24.77, 39.37) * mm, "end": v(-17.78, 35.34) * mm});
            skCircle(sketch, "E38.1.0.18", {"center": v(-24.77, 71.94) * mm, "radius": 6.99 * mm, "construction": true});
            skPoint(sketch, "E38.1.0.19", {"position": v(-24.77, 106.68) * mm});
            skLineSegment(sketch, "E38.1.0.20", {"start": v(-31.75, 67.91) * mm, "end": v(-31.75, 75.98) * mm});
            skCircle(sketch, "E38.1.0.21", {"center": v(-24.77, 92.26) * mm, "radius": 6.99 * mm, "construction": true});
            skLineSegment(sketch, "E38.1.0.22", {"start": v(-31.75, 116.62) * mm, "end": v(-24.77, 120.65) * mm});
            skLineSegment(sketch, "E38.1.0.23", {"start": v(-24.77, 63.88) * mm, "end": v(-31.75, 67.91) * mm});
            skLineSegment(sketch, "E38.1.0.24", {"start": v(-31.75, 6.95) * mm, "end": v(-31.75, 15.02) * mm});
            skLineSegment(sketch, "E38.1.0.25", {"start": v(-24.77, 2.92) * mm, "end": v(-31.75, 6.95) * mm});
            skPoint(sketch, "E38.1.0.26", {"position": v(-24.77, 127) * mm});
            skLineSegment(sketch, "E38.1.0.27", {"start": v(-24.77, 59.7) * mm, "end": v(-17.78, 55.66) * mm});
            skLineSegment(sketch, "E38.1.0.28", {"start": v(-31.75, 96.3) * mm, "end": v(-24.77, 100.33) * mm});
            skLineSegment(sketch, "E38.1.0.29", {"start": v(-24.77, 127) * mm, "end": v(-24.77, 112.58) * mm});
            skCircle(sketch, "E38.1.0.30", {"center": v(-24.77, 112.58) * mm, "radius": 6.99 * mm, "construction": true});
            skPoint(sketch, "E38.1.0.31", {"position": v(-24.77, 45.72) * mm});
            skLineSegment(sketch, "E38.1.0.32", {"start": v(-31.75, 15.02) * mm, "end": v(-24.77, 19.05) * mm});
            skLineSegment(sketch, "E38.1.0.33", {"start": v(-31.75, 88.23) * mm, "end": v(-31.75, 96.3) * mm});
            skLineSegment(sketch, "E38.1.0.34", {"start": v(-24.77, 100.33) * mm, "end": v(-17.78, 96.3) * mm});
            skLineSegment(sketch, "E38.1.0.35", {"start": v(-17.78, 116.62) * mm, "end": v(-17.78, 108.55) * mm});
            skLineSegment(sketch, "E38.1.0.36", {"start": v(-24.77, 120.65) * mm, "end": v(-17.78, 116.62) * mm});
            skLineSegment(sketch, "E38.1.0.37", {"start": v(-31.75, 55.66) * mm, "end": v(-24.77, 59.7) * mm});
            skLineSegment(sketch, "E38.1.0.38", {"start": v(-17.78, 15.02) * mm, "end": v(-17.78, 6.95) * mm});
            skLineSegment(sketch, "E38.1.0.39", {"start": v(-17.78, 67.91) * mm, "end": v(-24.77, 63.88) * mm});
            skLineSegment(sketch, "E38.1.0.40", {"start": v(-17.78, 108.55) * mm, "end": v(-24.76, 104.52) * mm});
            skLineSegment(sketch, "E38.1.0.41", {"start": v(-17.78, 75.98) * mm, "end": v(-17.78, 67.91) * mm});
            skLineSegment(sketch, "E38.1.0.42", {"start": v(-17.78, 35.34) * mm, "end": v(-17.78, 27.27) * mm});
            skLineSegment(sketch, "E38.1.0.43", {"start": v(-17.78, 96.3) * mm, "end": v(-17.78, 88.23) * mm});
            skLineSegment(sketch, "E38.1.0.44", {"start": v(-24.77, 23.24) * mm, "end": v(-31.75, 27.27) * mm});
            skLineSegment(sketch, "E38.1.0.45", {"start": v(-17.78, 27.27) * mm, "end": v(-24.76, 23.24) * mm});
            skLineSegment(sketch, "E38.1.0.46", {"start": v(-24.77, 43.56) * mm, "end": v(-31.75, 47.6) * mm});
            skLineSegment(sketch, "E38.1.0.47", {"start": v(-17.78, 55.66) * mm, "end": v(-17.78, 47.6) * mm});
            skLineSegment(sketch, "E38.1.0.48", {"start": v(-24.77, 84.2) * mm, "end": v(-31.75, 88.23) * mm});
            skLineSegment(sketch, "E38.1.0.49", {"start": v(-17.78, 47.6) * mm, "end": v(-24.77, 43.56) * mm});
            skLineSegment(sketch, "E38.direction1", {"start": v(-6.99, 6.95) * mm, "end": v(-31.75, 6.95) * mm, "construction": true});
            skSolve(sketch);
        }
        {
            var Q0;
            Q0 = qSketchRegion(id + "F5", true);
            extrude(context, id + "F6", {"entities" : qUnion([Q0]), "operationType" : NewBodyOperationType.REMOVE, "endBound" : BoundingType.SYMMETRIC, "oppositeDirection" : true, "depth" : 114.3 * mm, "offsetDistance" : 25.4 * mm});
        }
        {
            var Q0;
            Q0=makeQuery(id+"F3.boolean.opBoolean","MERGE",EDGE,{"derivedFrom":[makeQuery(id+"F1.opExtrude","SWEPT_EDGE",EDGE,{"disambiguationData":[OSD([sQuery(id+"F0.wireOp",EDGE,"E14.0"),sQuery(id+"F0.wireOp",EDGE,"E14.1")])]}),makeQuery(id+"F3.opExtrude","SWEPT_EDGE",EDGE,{"disambiguationData":[OSD([sQuery(id+"F2.wireOp",EDGE,"E15"),sQuery(id+"F2.wireOp",EDGE,"E16")])]})]});
            var Q1;
            Q1=makeQuery(id+"F3.boolean.opBoolean","MERGE",EDGE,{"derivedFrom":[makeQuery(id+"F1.opExtrude","SWEPT_EDGE",EDGE,{"disambiguationData":[OSD([sQuery(id+"F0.wireOp",EDGE,"E14.14"),sQuery(id+"F0.wireOp",EDGE,"E14.15")])]}),makeQuery(id+"F3.opExtrude","SWEPT_EDGE",EDGE,{"disambiguationData":[OSD([sQuery(id+"F2.wireOp",EDGE,"E24"),sQuery(id+"F2.wireOp",EDGE,"E25")])]})]});
            cPlane(context, id + "F7", {"entities" : qUnion([Q0, Q1]), "cplaneType" : CPlaneType.LINE_ANGLE, "offset" : 25.4 * mm, "angle" : 0 * degree, "width" : 152.4 * mm, "height" : 152.4 * mm});
        }
        {
            var Q0;
            Q0=qCreatedBy(id+"F7.planeOp",FACE);
            var sketch = newSketch(context, id + "F8", { "sketchPlane" : qUnion([Q0])});
            skCircle(sketch, "E39.cCircle", {"center": v(0, 112.58) * mm, "radius": 6.99 * mm, "construction": true});
            skPoint(sketch, "E39.cCircle.centerSnap0", {"position": v(0, 127) * mm});
            skLineSegment(sketch, "E39.0", {"start": v(-6.98, 108.55) * mm, "end": v(-6.98, 116.62) * mm});
            skLineSegment(sketch, "E39.1", {"start": v(-6.98, 116.62) * mm, "end": v(0, 120.65) * mm});
            skLineSegment(sketch, "E39.2", {"start": v(0, 120.65) * mm, "end": v(6.99, 116.62) * mm});
            skLineSegment(sketch, "E39.3", {"start": v(6.99, 116.62) * mm, "end": v(6.99, 108.55) * mm});
            skLineSegment(sketch, "E39.4", {"start": v(6.99, 108.55) * mm, "end": v(0, 104.52) * mm});
            skLineSegment(sketch, "E39.5", {"start": v(0, 104.52) * mm, "end": v(-6.98, 108.55) * mm});
            skPoint(sketch, "E40.1.0.0", {"position": v(0, 106.68) * mm});
            skLineSegment(sketch, "E40.1.0.1", {"start": v(6.99, 96.3) * mm, "end": v(6.99, 88.23) * mm});
            skCircle(sketch, "E40.1.0.3", {"center": v(0, 92.26) * mm, "radius": 6.99 * mm, "construction": true});
            skLineSegment(sketch, "E40.1.0.4", {"start": v(0, 100.33) * mm, "end": v(6.98, 96.3) * mm});
            skLineSegment(sketch, "E40.1.0.5", {"start": v(-6.98, 96.3) * mm, "end": v(0, 100.33) * mm});
            skLineSegment(sketch, "E40.1.0.6", {"start": v(-6.98, 88.23) * mm, "end": v(-6.98, 96.3) * mm});
            skLineSegment(sketch, "E40.1.0.7", {"start": v(0, 84.2) * mm, "end": v(-6.98, 88.23) * mm});
            skLineSegment(sketch, "E40.1.0.8", {"start": v(6.99, 88.23) * mm, "end": v(0, 84.2) * mm});
            skPoint(sketch, "E40.2.0.0", {"position": v(0, 86.36) * mm});
            skLineSegment(sketch, "E40.2.0.1", {"start": v(6.99, 75.98) * mm, "end": v(6.99, 67.91) * mm});
            skCircle(sketch, "E40.2.0.3", {"center": v(0, 71.94) * mm, "radius": 6.99 * mm, "construction": true});
            skLineSegment(sketch, "E40.2.0.4", {"start": v(0, 80.01) * mm, "end": v(6.99, 75.98) * mm});
            skLineSegment(sketch, "E40.2.0.5", {"start": v(-6.98, 75.98) * mm, "end": v(0, 80) * mm});
            skLineSegment(sketch, "E40.2.0.6", {"start": v(-6.98, 67.91) * mm, "end": v(-6.98, 75.98) * mm});
            skLineSegment(sketch, "E40.2.0.7", {"start": v(0, 63.88) * mm, "end": v(-6.98, 67.91) * mm});
            skLineSegment(sketch, "E40.2.0.8", {"start": v(6.99, 67.91) * mm, "end": v(0, 63.88) * mm});
            skPoint(sketch, "E40.3.0.0", {"position": v(0, 66.04) * mm});
            skLineSegment(sketch, "E40.3.0.1", {"start": v(6.99, 55.66) * mm, "end": v(6.99, 47.6) * mm});
            skCircle(sketch, "E40.3.0.3", {"center": v(0, 51.62) * mm, "radius": 6.99 * mm, "construction": true});
            skLineSegment(sketch, "E40.3.0.4", {"start": v(0, 59.7) * mm, "end": v(6.99, 55.66) * mm});
            skLineSegment(sketch, "E40.3.0.5", {"start": v(-6.98, 55.66) * mm, "end": v(0, 59.69) * mm});
            skLineSegment(sketch, "E40.3.0.6", {"start": v(-6.98, 47.6) * mm, "end": v(-6.98, 55.66) * mm});
            skLineSegment(sketch, "E40.3.0.7", {"start": v(0, 43.56) * mm, "end": v(-6.98, 47.6) * mm});
            skLineSegment(sketch, "E40.3.0.8", {"start": v(6.99, 47.6) * mm, "end": v(0, 43.56) * mm});
            skPoint(sketch, "E40.4.0.0", {"position": v(0, 45.72) * mm});
            skLineSegment(sketch, "E40.4.0.1", {"start": v(6.99, 35.34) * mm, "end": v(6.99, 27.27) * mm});
            skCircle(sketch, "E40.4.0.3", {"center": v(0, 31.3) * mm, "radius": 6.99 * mm, "construction": true});
            skLineSegment(sketch, "E40.4.0.4", {"start": v(0, 39.37) * mm, "end": v(6.99, 35.34) * mm});
            skLineSegment(sketch, "E40.4.0.5", {"start": v(-6.98, 35.34) * mm, "end": v(0, 39.37) * mm});
            skLineSegment(sketch, "E40.4.0.6", {"start": v(-6.98, 27.27) * mm, "end": v(-6.98, 35.34) * mm});
            skLineSegment(sketch, "E40.4.0.7", {"start": v(0, 23.24) * mm, "end": v(-6.98, 27.27) * mm});
            skLineSegment(sketch, "E40.4.0.8", {"start": v(6.99, 27.27) * mm, "end": v(0, 23.24) * mm});
            skLineSegment(sketch, "E40.direction1", {"start": v(-6.98, 108.55) * mm, "end": v(-6.98, 88.23) * mm, "construction": true});
            skPoint(sketch, "E41.0.5.0", {"position": v(0, 25.4) * mm});
            skLineSegment(sketch, "E41.1.5.0", {"start": v(6.99, 15.02) * mm, "end": v(6.99, 6.95) * mm});
            skCircle(sketch, "E41.5.5.0", {"center": v(0, 10.98) * mm, "radius": 6.99 * mm, "construction": true});
            skLineSegment(sketch, "E41.7.5.0", {"start": v(0, 19.05) * mm, "end": v(6.99, 15.02) * mm});
            skLineSegment(sketch, "E41.10.5.0", {"start": v(-6.98, 15.02) * mm, "end": v(0, 19.05) * mm});
            skLineSegment(sketch, "E41.13.5.0", {"start": v(-6.98, 6.95) * mm, "end": v(-6.98, 15.02) * mm});
            skLineSegment(sketch, "E41.16.5.0", {"start": v(0, 2.92) * mm, "end": v(-6.98, 6.95) * mm});
            skLineSegment(sketch, "E41.19.5.0", {"start": v(6.99, 6.95) * mm, "end": v(0, 2.92) * mm});
            skLineSegment(sketch, "E42", {"start": v(0, 127) * mm, "end": v(0, 112.58) * mm});
            skCircle(sketch, "E43.1.0.0", {"center": v(24.76, 112.58) * mm, "radius": 6.99 * mm, "construction": true});
            skPoint(sketch, "E43.1.0.1", {"position": v(24.76, 86.36) * mm});
            skCircle(sketch, "E43.1.0.2", {"center": v(24.76, 71.94) * mm, "radius": 6.99 * mm, "construction": true});
            skLineSegment(sketch, "E43.1.0.3", {"start": v(17.78, 96.3) * mm, "end": v(24.76, 100.33) * mm});
            skPoint(sketch, "E43.1.0.4", {"position": v(24.76, 106.68) * mm});
            skLineSegment(sketch, "E43.1.0.5", {"start": v(31.75, 55.66) * mm, "end": v(31.75, 47.6) * mm});
            skLineSegment(sketch, "E43.1.0.6", {"start": v(24.76, 127) * mm, "end": v(24.76, 112.58) * mm});
            skPoint(sketch, "E43.1.0.7", {"position": v(24.76, 45.72) * mm});
            skLineSegment(sketch, "E43.1.0.8", {"start": v(31.75, 108.55) * mm, "end": v(24.77, 104.52) * mm});
            skLineSegment(sketch, "E43.1.0.9", {"start": v(17.78, 6.95) * mm, "end": v(17.78, 15.02) * mm});
            skCircle(sketch, "E43.1.0.10", {"center": v(24.76, 51.62) * mm, "radius": 6.99 * mm, "construction": true});
            skCircle(sketch, "E43.1.0.11", {"center": v(24.76, 10.98) * mm, "radius": 6.99 * mm, "construction": true});
            skLineSegment(sketch, "E43.1.0.12", {"start": v(17.78, 108.55) * mm, "end": v(17.78, 88.23) * mm, "construction": true});
            skLineSegment(sketch, "E43.1.0.13", {"start": v(24.77, 39.37) * mm, "end": v(31.75, 35.34) * mm});
            skLineSegment(sketch, "E43.1.0.14", {"start": v(31.75, 6.95) * mm, "end": v(24.77, 2.92) * mm});
            skLineSegment(sketch, "E43.1.0.15", {"start": v(17.78, 116.62) * mm, "end": v(24.77, 120.65) * mm});
            skLineSegment(sketch, "E43.1.0.16", {"start": v(17.78, 55.66) * mm, "end": v(24.76, 59.69) * mm});
            skCircle(sketch, "E43.1.0.17", {"center": v(24.76, 92.26) * mm, "radius": 6.99 * mm, "construction": true});
            skLineSegment(sketch, "E43.1.0.18", {"start": v(17.78, 15.02) * mm, "end": v(24.77, 19.05) * mm});
            skLineSegment(sketch, "E43.1.0.19", {"start": v(24.77, 84.2) * mm, "end": v(17.78, 88.23) * mm});
            skPoint(sketch, "E43.1.0.20", {"position": v(24.76, 25.4) * mm});
            skPoint(sketch, "E43.1.0.21", {"position": v(24.76, 66.04) * mm});
            skCircle(sketch, "E43.1.0.22", {"center": v(24.76, 31.3) * mm, "radius": 6.99 * mm, "construction": true});
            skLineSegment(sketch, "E43.1.0.23", {"start": v(24.77, 43.56) * mm, "end": v(17.78, 47.6) * mm});
            skLineSegment(sketch, "E43.1.0.24", {"start": v(31.75, 27.27) * mm, "end": v(24.77, 23.24) * mm});
            skLineSegment(sketch, "E43.1.0.25", {"start": v(31.75, 67.91) * mm, "end": v(24.77, 63.88) * mm});
            skLineSegment(sketch, "E43.1.0.26", {"start": v(17.78, 27.27) * mm, "end": v(17.78, 35.34) * mm});
            skLineSegment(sketch, "E43.1.0.27", {"start": v(24.77, 63.88) * mm, "end": v(17.78, 67.91) * mm});
            skLineSegment(sketch, "E43.1.0.28", {"start": v(24.77, 120.65) * mm, "end": v(31.75, 116.62) * mm});
            skLineSegment(sketch, "E43.1.0.29", {"start": v(17.78, 88.23) * mm, "end": v(17.78, 96.3) * mm});
            skLineSegment(sketch, "E43.1.0.30", {"start": v(24.77, 2.92) * mm, "end": v(17.78, 6.95) * mm});
            skLineSegment(sketch, "E43.1.0.31", {"start": v(31.75, 96.3) * mm, "end": v(31.75, 88.23) * mm});
            skLineSegment(sketch, "E43.1.0.32", {"start": v(31.75, 47.6) * mm, "end": v(24.77, 43.56) * mm});
            skLineSegment(sketch, "E43.1.0.33", {"start": v(24.77, 23.24) * mm, "end": v(17.78, 27.27) * mm});
            skLineSegment(sketch, "E43.1.0.34", {"start": v(24.77, 59.7) * mm, "end": v(31.75, 55.66) * mm});
            skLineSegment(sketch, "E43.1.0.35", {"start": v(17.78, 35.34) * mm, "end": v(24.76, 39.37) * mm});
            skLineSegment(sketch, "E43.1.0.36", {"start": v(17.78, 67.91) * mm, "end": v(17.78, 75.98) * mm});
            skLineSegment(sketch, "E43.1.0.37", {"start": v(31.75, 75.98) * mm, "end": v(31.75, 67.91) * mm});
            skLineSegment(sketch, "E43.1.0.38", {"start": v(17.78, 108.55) * mm, "end": v(17.78, 116.62) * mm});
            skLineSegment(sketch, "E43.1.0.39", {"start": v(31.75, 88.23) * mm, "end": v(24.77, 84.2) * mm});
            skLineSegment(sketch, "E43.1.0.40", {"start": v(24.77, 104.52) * mm, "end": v(17.78, 108.55) * mm});
            skLineSegment(sketch, "E43.1.0.41", {"start": v(17.78, 75.98) * mm, "end": v(24.76, 80) * mm});
            skLineSegment(sketch, "E43.1.0.42", {"start": v(31.75, 116.62) * mm, "end": v(31.75, 108.55) * mm});
            skLineSegment(sketch, "E43.1.0.43", {"start": v(24.77, 80.01) * mm, "end": v(31.75, 75.98) * mm});
            skLineSegment(sketch, "E43.1.0.44", {"start": v(24.77, 100.33) * mm, "end": v(31.75, 96.3) * mm});
            skLineSegment(sketch, "E43.1.0.45", {"start": v(24.77, 19.05) * mm, "end": v(31.75, 15.02) * mm});
            skLineSegment(sketch, "E43.1.0.46", {"start": v(31.75, 15.02) * mm, "end": v(31.75, 6.95) * mm});
            skLineSegment(sketch, "E43.1.0.47", {"start": v(31.75, 35.34) * mm, "end": v(31.75, 27.27) * mm});
            skLineSegment(sketch, "E43.1.0.48", {"start": v(17.78, 47.6) * mm, "end": v(17.78, 55.66) * mm});
            skLineSegment(sketch, "E43.direction1", {"start": v(-6.98, 6.95) * mm, "end": v(17.78, 6.95) * mm, "construction": true});
            skPoint(sketch, "E44.1.0.0", {"position": v(-24.77, 25.4) * mm});
            skLineSegment(sketch, "E44.1.0.1", {"start": v(-24.76, 104.52) * mm, "end": v(-31.75, 108.55) * mm});
            skLineSegment(sketch, "E44.1.0.2", {"start": v(-17.78, 88.23) * mm, "end": v(-24.76, 84.2) * mm});
            skLineSegment(sketch, "E44.1.0.3", {"start": v(-17.78, 6.95) * mm, "end": v(-24.76, 2.92) * mm});
            skLineSegment(sketch, "E44.1.0.4", {"start": v(-31.75, 27.27) * mm, "end": v(-31.75, 35.34) * mm});
            skLineSegment(sketch, "E44.1.0.5", {"start": v(-31.75, 108.55) * mm, "end": v(-31.75, 88.23) * mm, "construction": true});
            skLineSegment(sketch, "E44.1.0.6", {"start": v(-31.75, 108.55) * mm, "end": v(-31.75, 116.62) * mm});
            skLineSegment(sketch, "E44.1.0.7", {"start": v(-24.76, 19.05) * mm, "end": v(-17.78, 15.02) * mm});
            skLineSegment(sketch, "E44.1.0.8", {"start": v(-24.76, 80.01) * mm, "end": v(-17.78, 75.98) * mm});
            skPoint(sketch, "E44.1.0.9", {"position": v(-24.77, 86.36) * mm});
            skLineSegment(sketch, "E44.1.0.10", {"start": v(-31.75, 47.6) * mm, "end": v(-31.75, 55.66) * mm});
            skCircle(sketch, "E44.1.0.11", {"center": v(-24.77, 51.62) * mm, "radius": 6.99 * mm, "construction": true});
            skPoint(sketch, "E44.1.0.12", {"position": v(-24.77, 66.04) * mm});
            skLineSegment(sketch, "E44.1.0.13", {"start": v(-31.75, 75.98) * mm, "end": v(-24.76, 80) * mm});
            skLineSegment(sketch, "E44.1.0.14", {"start": v(-31.75, 35.34) * mm, "end": v(-24.76, 39.37) * mm});
            skCircle(sketch, "E44.1.0.15", {"center": v(-24.77, 31.3) * mm, "radius": 6.99 * mm, "construction": true});
            skCircle(sketch, "E44.1.0.16", {"center": v(-24.77, 10.98) * mm, "radius": 6.99 * mm, "construction": true});
            skLineSegment(sketch, "E44.1.0.17", {"start": v(-24.76, 39.37) * mm, "end": v(-17.78, 35.34) * mm});
            skCircle(sketch, "E44.1.0.18", {"center": v(-24.77, 71.94) * mm, "radius": 6.99 * mm, "construction": true});
            skPoint(sketch, "E44.1.0.19", {"position": v(-24.77, 106.68) * mm});
            skLineSegment(sketch, "E44.1.0.20", {"start": v(-31.75, 67.91) * mm, "end": v(-31.75, 75.98) * mm});
            skCircle(sketch, "E44.1.0.21", {"center": v(-24.77, 92.26) * mm, "radius": 6.99 * mm, "construction": true});
            skLineSegment(sketch, "E44.1.0.22", {"start": v(-31.75, 116.62) * mm, "end": v(-24.76, 120.65) * mm});
            skLineSegment(sketch, "E44.1.0.23", {"start": v(-24.76, 63.88) * mm, "end": v(-31.75, 67.91) * mm});
            skLineSegment(sketch, "E44.1.0.24", {"start": v(-31.75, 6.95) * mm, "end": v(-31.75, 15.02) * mm});
            skLineSegment(sketch, "E44.1.0.25", {"start": v(-24.76, 2.92) * mm, "end": v(-31.75, 6.95) * mm});
            skPoint(sketch, "E44.1.0.26", {"position": v(-24.77, 127) * mm});
            skLineSegment(sketch, "E44.1.0.27", {"start": v(-24.77, 59.7) * mm, "end": v(-17.78, 55.66) * mm});
            skLineSegment(sketch, "E44.1.0.28", {"start": v(-31.75, 96.3) * mm, "end": v(-24.76, 100.33) * mm});
            skLineSegment(sketch, "E44.1.0.29", {"start": v(-24.76, 127) * mm, "end": v(-24.76, 112.58) * mm});
            skCircle(sketch, "E44.1.0.30", {"center": v(-24.77, 112.58) * mm, "radius": 6.99 * mm, "construction": true});
            skPoint(sketch, "E44.1.0.31", {"position": v(-24.77, 45.72) * mm});
            skLineSegment(sketch, "E44.1.0.32", {"start": v(-31.75, 15.02) * mm, "end": v(-24.76, 19.05) * mm});
            skLineSegment(sketch, "E44.1.0.33", {"start": v(-31.75, 88.23) * mm, "end": v(-31.75, 96.3) * mm});
            skLineSegment(sketch, "E44.1.0.34", {"start": v(-24.77, 100.33) * mm, "end": v(-17.78, 96.3) * mm});
            skLineSegment(sketch, "E44.1.0.35", {"start": v(-17.78, 116.62) * mm, "end": v(-17.78, 108.55) * mm});
            skLineSegment(sketch, "E44.1.0.36", {"start": v(-24.77, 120.65) * mm, "end": v(-17.78, 116.62) * mm});
            skLineSegment(sketch, "E44.1.0.37", {"start": v(-31.75, 55.66) * mm, "end": v(-24.76, 59.69) * mm});
            skLineSegment(sketch, "E44.1.0.38", {"start": v(-17.78, 15.02) * mm, "end": v(-17.78, 6.95) * mm});
            skLineSegment(sketch, "E44.1.0.39", {"start": v(-17.78, 67.91) * mm, "end": v(-24.76, 63.88) * mm});
            skLineSegment(sketch, "E44.1.0.40", {"start": v(-17.78, 108.55) * mm, "end": v(-24.76, 104.52) * mm});
            skLineSegment(sketch, "E44.1.0.41", {"start": v(-17.78, 75.98) * mm, "end": v(-17.78, 67.91) * mm});
            skLineSegment(sketch, "E44.1.0.42", {"start": v(-17.78, 35.34) * mm, "end": v(-17.78, 27.27) * mm});
            skLineSegment(sketch, "E44.1.0.43", {"start": v(-17.78, 96.3) * mm, "end": v(-17.78, 88.23) * mm});
            skLineSegment(sketch, "E44.1.0.44", {"start": v(-24.76, 23.24) * mm, "end": v(-31.75, 27.27) * mm});
            skLineSegment(sketch, "E44.1.0.45", {"start": v(-17.78, 27.27) * mm, "end": v(-24.76, 23.24) * mm});
            skLineSegment(sketch, "E44.1.0.46", {"start": v(-24.76, 43.56) * mm, "end": v(-31.75, 47.6) * mm});
            skLineSegment(sketch, "E44.1.0.47", {"start": v(-17.78, 55.66) * mm, "end": v(-17.78, 47.6) * mm});
            skLineSegment(sketch, "E44.1.0.48", {"start": v(-24.76, 84.2) * mm, "end": v(-31.75, 88.23) * mm});
            skLineSegment(sketch, "E44.1.0.49", {"start": v(-17.78, 47.6) * mm, "end": v(-24.76, 43.56) * mm});
            skLineSegment(sketch, "E44.direction1", {"start": v(-6.98, 6.95) * mm, "end": v(-31.75, 6.95) * mm, "construction": true});
            skSolve(sketch);
        }
        {
            var Q0;
            Q0=makeQuery(id+"F3.boolean.opBoolean","MERGE",EDGE,{"derivedFrom":[makeQuery(id+"F1.opExtrude","SWEPT_EDGE",EDGE,{"disambiguationData":[OSD([sQuery(id+"F0.wireOp",EDGE,"E14.3"),sQuery(id+"F0.wireOp",EDGE,"E14.4")])]}),makeQuery(id+"F3.opExtrude","SWEPT_EDGE",EDGE,{"disambiguationData":[OSD([sQuery(id+"F2.wireOp",EDGE,"E30"),sQuery(id+"F2.wireOp",EDGE,"E31")])]})]});
            var Q1;
            Q1=makeQuery(id+"F3.boolean.opBoolean","MERGE",EDGE,{"derivedFrom":[makeQuery(id+"F1.opExtrude","SWEPT_EDGE",EDGE,{"disambiguationData":[OSD([sQuery(id+"F0.wireOp",EDGE,"E14.8"),sQuery(id+"F0.wireOp",EDGE,"E14.12")])]}),makeQuery(id+"F3.opExtrude","SWEPT_EDGE",EDGE,{"disambiguationData":[OSD([sQuery(id+"F2.wireOp",EDGE,"E21"),sQuery(id+"F2.wireOp",EDGE,"E22")])]})]});
            cPlane(context, id + "F9", {"entities" : qUnion([Q0, Q1]), "cplaneType" : CPlaneType.LINE_ANGLE, "offset" : 25.4 * mm, "angle" : 0 * degree, "width" : 152.4 * mm, "height" : 152.4 * mm});
        }
        {
            var Q0;
            Q0=qCreatedBy(id+"F9.planeOp",FACE);
            var sketch = newSketch(context, id + "F10", { "sketchPlane" : qUnion([Q0])});
            skCircle(sketch, "E45.cCircle", {"center": v(0, 112.58) * mm, "radius": 6.99 * mm, "construction": true});
            skPoint(sketch, "E45.cCircle.centerSnap0", {"position": v(0, 127) * mm});
            skLineSegment(sketch, "E45.0", {"start": v(-6.99, 108.55) * mm, "end": v(-6.99, 116.62) * mm});
            skLineSegment(sketch, "E45.1", {"start": v(-6.99, 116.62) * mm, "end": v(0, 120.65) * mm});
            skLineSegment(sketch, "E45.2", {"start": v(0, 120.65) * mm, "end": v(6.99, 116.62) * mm});
            skLineSegment(sketch, "E45.3", {"start": v(6.99, 116.62) * mm, "end": v(6.99, 108.55) * mm});
            skLineSegment(sketch, "E45.4", {"start": v(6.99, 108.55) * mm, "end": v(0, 104.52) * mm});
            skLineSegment(sketch, "E45.5", {"start": v(0, 104.52) * mm, "end": v(-6.99, 108.55) * mm});
            skPoint(sketch, "E46.1.0.0", {"position": v(0, 106.68) * mm});
            skLineSegment(sketch, "E46.1.0.1", {"start": v(6.99, 96.3) * mm, "end": v(6.99, 88.23) * mm});
            skCircle(sketch, "E46.1.0.3", {"center": v(0, 92.26) * mm, "radius": 6.99 * mm, "construction": true});
            skLineSegment(sketch, "E46.1.0.4", {"start": v(0, 100.33) * mm, "end": v(6.98, 96.3) * mm});
            skLineSegment(sketch, "E46.1.0.5", {"start": v(-6.99, 96.3) * mm, "end": v(0, 100.33) * mm});
            skLineSegment(sketch, "E46.1.0.6", {"start": v(-6.99, 88.23) * mm, "end": v(-6.99, 96.3) * mm});
            skLineSegment(sketch, "E46.1.0.7", {"start": v(0, 84.2) * mm, "end": v(-6.99, 88.23) * mm});
            skLineSegment(sketch, "E46.1.0.8", {"start": v(6.99, 88.23) * mm, "end": v(0, 84.2) * mm});
            skPoint(sketch, "E46.2.0.0", {"position": v(0, 86.36) * mm});
            skLineSegment(sketch, "E46.2.0.1", {"start": v(6.99, 75.98) * mm, "end": v(6.99, 67.91) * mm});
            skCircle(sketch, "E46.2.0.3", {"center": v(0, 71.94) * mm, "radius": 6.99 * mm, "construction": true});
            skLineSegment(sketch, "E46.2.0.4", {"start": v(0, 80) * mm, "end": v(6.98, 75.98) * mm});
            skLineSegment(sketch, "E46.2.0.5", {"start": v(-6.99, 75.98) * mm, "end": v(0, 80) * mm});
            skLineSegment(sketch, "E46.2.0.6", {"start": v(-6.99, 67.91) * mm, "end": v(-6.99, 75.98) * mm});
            skLineSegment(sketch, "E46.2.0.7", {"start": v(0, 63.88) * mm, "end": v(-6.98, 67.91) * mm});
            skLineSegment(sketch, "E46.2.0.8", {"start": v(6.99, 67.91) * mm, "end": v(0, 63.88) * mm});
            skPoint(sketch, "E46.3.0.0", {"position": v(0, 66.04) * mm});
            skLineSegment(sketch, "E46.3.0.1", {"start": v(6.99, 55.66) * mm, "end": v(6.99, 47.6) * mm});
            skCircle(sketch, "E46.3.0.3", {"center": v(0, 51.62) * mm, "radius": 6.99 * mm, "construction": true});
            skLineSegment(sketch, "E46.3.0.4", {"start": v(0, 59.69) * mm, "end": v(6.98, 55.66) * mm});
            skLineSegment(sketch, "E46.3.0.5", {"start": v(-6.99, 55.66) * mm, "end": v(0, 59.69) * mm});
            skLineSegment(sketch, "E46.3.0.6", {"start": v(-6.99, 47.6) * mm, "end": v(-6.99, 55.66) * mm});
            skLineSegment(sketch, "E46.3.0.7", {"start": v(0, 43.56) * mm, "end": v(-6.99, 47.6) * mm});
            skLineSegment(sketch, "E46.3.0.8", {"start": v(6.99, 47.6) * mm, "end": v(0, 43.56) * mm});
            skPoint(sketch, "E46.4.0.0", {"position": v(0, 45.72) * mm});
            skLineSegment(sketch, "E46.4.0.1", {"start": v(6.99, 35.34) * mm, "end": v(6.99, 27.27) * mm});
            skCircle(sketch, "E46.4.0.3", {"center": v(0, 31.3) * mm, "radius": 6.99 * mm, "construction": true});
            skLineSegment(sketch, "E46.4.0.4", {"start": v(0, 39.37) * mm, "end": v(6.98, 35.34) * mm});
            skLineSegment(sketch, "E46.4.0.5", {"start": v(-6.98, 35.34) * mm, "end": v(0, 39.37) * mm});
            skLineSegment(sketch, "E46.4.0.6", {"start": v(-6.99, 27.27) * mm, "end": v(-6.99, 35.34) * mm});
            skLineSegment(sketch, "E46.4.0.7", {"start": v(0, 23.24) * mm, "end": v(-6.98, 27.27) * mm});
            skLineSegment(sketch, "E46.4.0.8", {"start": v(6.99, 27.27) * mm, "end": v(0, 23.24) * mm});
            skLineSegment(sketch, "E46.direction1", {"start": v(-6.99, 108.55) * mm, "end": v(-6.99, 88.23) * mm, "construction": true});
            skPoint(sketch, "E47.0.5.0", {"position": v(0, 25.4) * mm});
            skLineSegment(sketch, "E47.1.5.0", {"start": v(6.99, 15.02) * mm, "end": v(6.99, 6.95) * mm});
            skCircle(sketch, "E47.5.5.0", {"center": v(0, 10.98) * mm, "radius": 6.99 * mm, "construction": true});
            skLineSegment(sketch, "E47.7.5.0", {"start": v(0, 19.05) * mm, "end": v(6.99, 15.02) * mm});
            skLineSegment(sketch, "E47.10.5.0", {"start": v(-6.99, 15.02) * mm, "end": v(0, 19.05) * mm});
            skLineSegment(sketch, "E47.13.5.0", {"start": v(-6.99, 6.95) * mm, "end": v(-6.99, 15.02) * mm});
            skLineSegment(sketch, "E47.16.5.0", {"start": v(0, 2.92) * mm, "end": v(-6.99, 6.95) * mm});
            skLineSegment(sketch, "E47.19.5.0", {"start": v(6.98, 6.95) * mm, "end": v(0, 2.92) * mm});
            skLineSegment(sketch, "E48", {"start": v(0, 127) * mm, "end": v(0, 112.58) * mm});
            skCircle(sketch, "E49.1.0.0", {"center": v(24.76, 112.58) * mm, "radius": 6.99 * mm, "construction": true});
            skPoint(sketch, "E49.1.0.1", {"position": v(24.76, 86.36) * mm});
            skCircle(sketch, "E49.1.0.2", {"center": v(24.76, 71.94) * mm, "radius": 6.99 * mm, "construction": true});
            skLineSegment(sketch, "E49.1.0.3", {"start": v(17.78, 96.3) * mm, "end": v(24.76, 100.33) * mm});
            skPoint(sketch, "E49.1.0.4", {"position": v(24.76, 106.68) * mm});
            skLineSegment(sketch, "E49.1.0.5", {"start": v(31.75, 55.66) * mm, "end": v(31.75, 47.6) * mm});
            skLineSegment(sketch, "E49.1.0.6", {"start": v(24.76, 127) * mm, "end": v(24.76, 112.58) * mm});
            skPoint(sketch, "E49.1.0.7", {"position": v(24.76, 45.72) * mm});
            skLineSegment(sketch, "E49.1.0.8", {"start": v(31.75, 108.55) * mm, "end": v(24.76, 104.52) * mm});
            skLineSegment(sketch, "E49.1.0.9", {"start": v(17.78, 6.95) * mm, "end": v(17.78, 15.02) * mm});
            skCircle(sketch, "E49.1.0.10", {"center": v(24.76, 51.62) * mm, "radius": 6.99 * mm, "construction": true});
            skCircle(sketch, "E49.1.0.11", {"center": v(24.76, 10.98) * mm, "radius": 6.99 * mm, "construction": true});
            skLineSegment(sketch, "E49.1.0.12", {"start": v(17.78, 108.55) * mm, "end": v(17.78, 88.23) * mm, "construction": true});
            skLineSegment(sketch, "E49.1.0.13", {"start": v(24.76, 39.37) * mm, "end": v(31.75, 35.34) * mm});
            skLineSegment(sketch, "E49.1.0.14", {"start": v(31.75, 6.95) * mm, "end": v(24.76, 2.92) * mm});
            skLineSegment(sketch, "E49.1.0.15", {"start": v(17.78, 116.62) * mm, "end": v(24.76, 120.65) * mm});
            skLineSegment(sketch, "E49.1.0.16", {"start": v(17.78, 55.66) * mm, "end": v(24.76, 59.69) * mm});
            skCircle(sketch, "E49.1.0.17", {"center": v(24.76, 92.26) * mm, "radius": 6.99 * mm, "construction": true});
            skLineSegment(sketch, "E49.1.0.18", {"start": v(17.78, 15.02) * mm, "end": v(24.77, 19.05) * mm});
            skLineSegment(sketch, "E49.1.0.19", {"start": v(24.76, 84.2) * mm, "end": v(17.78, 88.23) * mm});
            skPoint(sketch, "E49.1.0.20", {"position": v(24.76, 25.4) * mm});
            skPoint(sketch, "E49.1.0.21", {"position": v(24.76, 66.04) * mm});
            skCircle(sketch, "E49.1.0.22", {"center": v(24.76, 31.3) * mm, "radius": 6.99 * mm, "construction": true});
            skLineSegment(sketch, "E49.1.0.23", {"start": v(24.76, 43.56) * mm, "end": v(17.78, 47.6) * mm});
            skLineSegment(sketch, "E49.1.0.24", {"start": v(31.75, 27.27) * mm, "end": v(24.76, 23.24) * mm});
            skLineSegment(sketch, "E49.1.0.25", {"start": v(31.75, 67.91) * mm, "end": v(24.77, 63.88) * mm});
            skLineSegment(sketch, "E49.1.0.26", {"start": v(17.78, 27.27) * mm, "end": v(17.78, 35.34) * mm});
            skLineSegment(sketch, "E49.1.0.27", {"start": v(24.77, 63.88) * mm, "end": v(17.78, 67.91) * mm});
            skLineSegment(sketch, "E49.1.0.28", {"start": v(24.77, 120.65) * mm, "end": v(31.75, 116.62) * mm});
            skLineSegment(sketch, "E49.1.0.29", {"start": v(17.78, 88.23) * mm, "end": v(17.78, 96.3) * mm});
            skLineSegment(sketch, "E49.1.0.30", {"start": v(24.76, 2.92) * mm, "end": v(17.78, 6.95) * mm});
            skLineSegment(sketch, "E49.1.0.31", {"start": v(31.75, 96.3) * mm, "end": v(31.75, 88.23) * mm});
            skLineSegment(sketch, "E49.1.0.32", {"start": v(31.75, 47.6) * mm, "end": v(24.77, 43.56) * mm});
            skLineSegment(sketch, "E49.1.0.33", {"start": v(24.76, 23.24) * mm, "end": v(17.78, 27.27) * mm});
            skLineSegment(sketch, "E49.1.0.34", {"start": v(24.77, 59.69) * mm, "end": v(31.75, 55.66) * mm});
            skLineSegment(sketch, "E49.1.0.35", {"start": v(17.78, 35.34) * mm, "end": v(24.76, 39.37) * mm});
            skLineSegment(sketch, "E49.1.0.36", {"start": v(17.78, 67.91) * mm, "end": v(17.78, 75.98) * mm});
            skLineSegment(sketch, "E49.1.0.37", {"start": v(31.75, 75.98) * mm, "end": v(31.75, 67.91) * mm});
            skLineSegment(sketch, "E49.1.0.38", {"start": v(17.78, 108.55) * mm, "end": v(17.78, 116.62) * mm});
            skLineSegment(sketch, "E49.1.0.39", {"start": v(31.75, 88.23) * mm, "end": v(24.77, 84.2) * mm});
            skLineSegment(sketch, "E49.1.0.40", {"start": v(24.76, 104.52) * mm, "end": v(17.78, 108.55) * mm});
            skLineSegment(sketch, "E49.1.0.41", {"start": v(17.78, 75.98) * mm, "end": v(24.76, 80) * mm});
            skLineSegment(sketch, "E49.1.0.42", {"start": v(31.75, 116.62) * mm, "end": v(31.75, 108.55) * mm});
            skLineSegment(sketch, "E49.1.0.43", {"start": v(24.76, 80) * mm, "end": v(31.75, 75.98) * mm});
            skLineSegment(sketch, "E49.1.0.44", {"start": v(24.76, 100.33) * mm, "end": v(31.75, 96.3) * mm});
            skLineSegment(sketch, "E49.1.0.45", {"start": v(24.76, 19.05) * mm, "end": v(31.75, 15.02) * mm});
            skLineSegment(sketch, "E49.1.0.46", {"start": v(31.75, 15.02) * mm, "end": v(31.75, 6.95) * mm});
            skLineSegment(sketch, "E49.1.0.47", {"start": v(31.75, 35.34) * mm, "end": v(31.75, 27.27) * mm});
            skLineSegment(sketch, "E49.1.0.48", {"start": v(17.78, 47.6) * mm, "end": v(17.78, 55.66) * mm});
            skLineSegment(sketch, "E49.direction1", {"start": v(-6.99, 6.95) * mm, "end": v(17.78, 6.95) * mm, "construction": true});
            skPoint(sketch, "E50.1.0.0", {"position": v(-24.77, 25.4) * mm});
            skLineSegment(sketch, "E50.1.0.1", {"start": v(-24.76, 104.52) * mm, "end": v(-31.75, 108.55) * mm});
            skLineSegment(sketch, "E50.1.0.2", {"start": v(-17.78, 88.23) * mm, "end": v(-24.76, 84.2) * mm});
            skLineSegment(sketch, "E50.1.0.3", {"start": v(-17.78, 6.95) * mm, "end": v(-24.76, 2.92) * mm});
            skLineSegment(sketch, "E50.1.0.4", {"start": v(-31.75, 27.27) * mm, "end": v(-31.75, 35.34) * mm});
            skLineSegment(sketch, "E50.1.0.5", {"start": v(-31.75, 108.55) * mm, "end": v(-31.75, 88.23) * mm, "construction": true});
            skLineSegment(sketch, "E50.1.0.6", {"start": v(-31.75, 108.55) * mm, "end": v(-31.75, 116.62) * mm});
            skLineSegment(sketch, "E50.1.0.7", {"start": v(-24.77, 19.05) * mm, "end": v(-17.78, 15.02) * mm});
            skLineSegment(sketch, "E50.1.0.8", {"start": v(-24.77, 80) * mm, "end": v(-17.78, 75.98) * mm});
            skPoint(sketch, "E50.1.0.9", {"position": v(-24.77, 86.36) * mm});
            skLineSegment(sketch, "E50.1.0.10", {"start": v(-31.75, 47.6) * mm, "end": v(-31.75, 55.66) * mm});
            skCircle(sketch, "E50.1.0.11", {"center": v(-24.77, 51.62) * mm, "radius": 6.99 * mm, "construction": true});
            skPoint(sketch, "E50.1.0.12", {"position": v(-24.77, 66.04) * mm});
            skLineSegment(sketch, "E50.1.0.13", {"start": v(-31.75, 75.98) * mm, "end": v(-24.76, 80) * mm});
            skLineSegment(sketch, "E50.1.0.14", {"start": v(-31.75, 35.34) * mm, "end": v(-24.76, 39.37) * mm});
            skCircle(sketch, "E50.1.0.15", {"center": v(-24.77, 31.3) * mm, "radius": 6.99 * mm, "construction": true});
            skCircle(sketch, "E50.1.0.16", {"center": v(-24.77, 10.98) * mm, "radius": 6.99 * mm, "construction": true});
            skLineSegment(sketch, "E50.1.0.17", {"start": v(-24.76, 39.37) * mm, "end": v(-17.78, 35.34) * mm});
            skCircle(sketch, "E50.1.0.18", {"center": v(-24.77, 71.94) * mm, "radius": 6.99 * mm, "construction": true});
            skPoint(sketch, "E50.1.0.19", {"position": v(-24.77, 106.68) * mm});
            skLineSegment(sketch, "E50.1.0.20", {"start": v(-31.75, 67.91) * mm, "end": v(-31.75, 75.98) * mm});
            skCircle(sketch, "E50.1.0.21", {"center": v(-24.77, 92.26) * mm, "radius": 6.99 * mm, "construction": true});
            skLineSegment(sketch, "E50.1.0.22", {"start": v(-31.75, 116.62) * mm, "end": v(-24.76, 120.65) * mm});
            skLineSegment(sketch, "E50.1.0.23", {"start": v(-24.77, 63.88) * mm, "end": v(-31.75, 67.91) * mm});
            skLineSegment(sketch, "E50.1.0.24", {"start": v(-31.75, 6.95) * mm, "end": v(-31.75, 15.02) * mm});
            skLineSegment(sketch, "E50.1.0.25", {"start": v(-24.76, 2.92) * mm, "end": v(-31.75, 6.95) * mm});
            skPoint(sketch, "E50.1.0.26", {"position": v(-24.77, 127) * mm});
            skLineSegment(sketch, "E50.1.0.27", {"start": v(-24.76, 59.69) * mm, "end": v(-17.78, 55.66) * mm});
            skLineSegment(sketch, "E50.1.0.28", {"start": v(-31.75, 96.3) * mm, "end": v(-24.76, 100.33) * mm});
            skLineSegment(sketch, "E50.1.0.29", {"start": v(-24.77, 127) * mm, "end": v(-24.77, 112.58) * mm});
            skCircle(sketch, "E50.1.0.30", {"center": v(-24.77, 112.58) * mm, "radius": 6.99 * mm, "construction": true});
            skPoint(sketch, "E50.1.0.31", {"position": v(-24.77, 45.72) * mm});
            skLineSegment(sketch, "E50.1.0.32", {"start": v(-31.75, 15.02) * mm, "end": v(-24.76, 19.05) * mm});
            skLineSegment(sketch, "E50.1.0.33", {"start": v(-31.75, 88.23) * mm, "end": v(-31.75, 96.3) * mm});
            skLineSegment(sketch, "E50.1.0.34", {"start": v(-24.77, 100.33) * mm, "end": v(-17.78, 96.3) * mm});
            skLineSegment(sketch, "E50.1.0.35", {"start": v(-17.78, 116.62) * mm, "end": v(-17.78, 108.55) * mm});
            skLineSegment(sketch, "E50.1.0.36", {"start": v(-24.77, 120.65) * mm, "end": v(-17.78, 116.62) * mm});
            skLineSegment(sketch, "E50.1.0.37", {"start": v(-31.75, 55.66) * mm, "end": v(-24.77, 59.69) * mm});
            skLineSegment(sketch, "E50.1.0.38", {"start": v(-17.78, 15.02) * mm, "end": v(-17.78, 6.95) * mm});
            skLineSegment(sketch, "E50.1.0.39", {"start": v(-17.78, 67.91) * mm, "end": v(-24.76, 63.88) * mm});
            skLineSegment(sketch, "E50.1.0.40", {"start": v(-17.78, 108.55) * mm, "end": v(-24.76, 104.52) * mm});
            skLineSegment(sketch, "E50.1.0.41", {"start": v(-17.78, 75.98) * mm, "end": v(-17.78, 67.91) * mm});
            skLineSegment(sketch, "E50.1.0.42", {"start": v(-17.78, 35.34) * mm, "end": v(-17.78, 27.27) * mm});
            skLineSegment(sketch, "E50.1.0.43", {"start": v(-17.78, 96.3) * mm, "end": v(-17.78, 88.23) * mm});
            skLineSegment(sketch, "E50.1.0.44", {"start": v(-24.76, 23.24) * mm, "end": v(-31.75, 27.27) * mm});
            skLineSegment(sketch, "E50.1.0.45", {"start": v(-17.78, 27.27) * mm, "end": v(-24.76, 23.24) * mm});
            skLineSegment(sketch, "E50.1.0.46", {"start": v(-24.76, 43.56) * mm, "end": v(-31.75, 47.6) * mm});
            skLineSegment(sketch, "E50.1.0.47", {"start": v(-17.78, 55.66) * mm, "end": v(-17.78, 47.6) * mm});
            skLineSegment(sketch, "E50.1.0.48", {"start": v(-24.77, 84.2) * mm, "end": v(-31.75, 88.23) * mm});
            skLineSegment(sketch, "E50.1.0.49", {"start": v(-17.78, 47.6) * mm, "end": v(-24.76, 43.56) * mm});
            skLineSegment(sketch, "E50.direction1", {"start": v(-6.99, 6.95) * mm, "end": v(-31.75, 6.95) * mm, "construction": true});
            skSolve(sketch);
        }
        {
            var Q0;
            Q0 = qSketchRegion(id + "F8", true);
            extrude(context, id + "F11", {"entities" : qUnion([Q0]), "operationType" : NewBodyOperationType.REMOVE, "endBound" : BoundingType.SYMMETRIC, "depth" : 101.6 * mm, "offsetDistance" : 25.4 * mm});
        }
        {
            var Q0;
            Q0 = qSketchRegion(id + "F10", true);
            extrude(context, id + "F12", {"entities" : qUnion([Q0]), "operationType" : NewBodyOperationType.REMOVE, "endBound" : BoundingType.SYMMETRIC, "oppositeDirection" : true, "depth" : 101.6 * mm, "offsetDistance" : 25.4 * mm});
        }
    });
